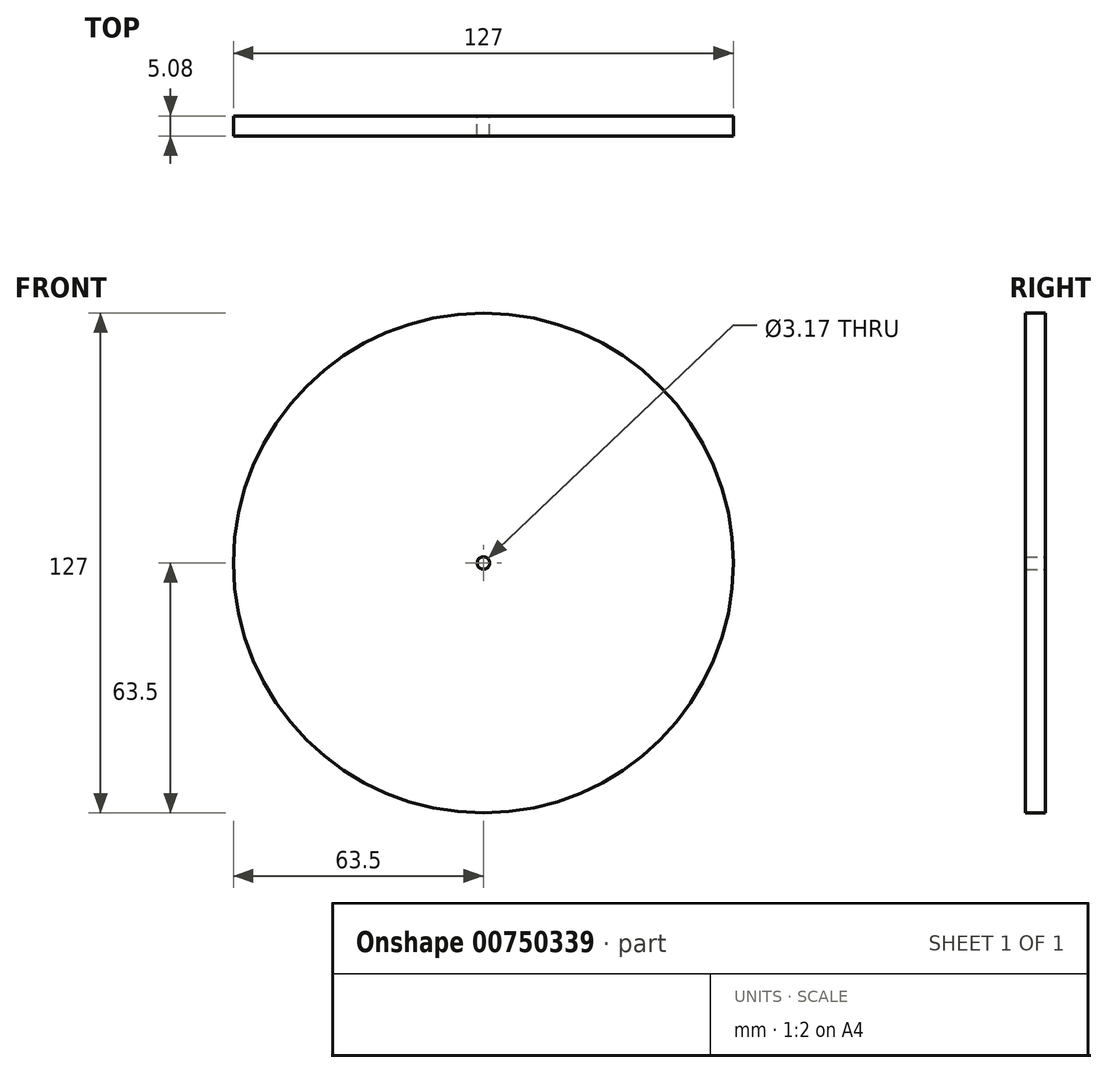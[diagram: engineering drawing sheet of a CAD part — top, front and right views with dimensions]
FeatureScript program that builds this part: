
annotation { "Feature Type Name" : "Feature", "Feature Type Description" : "" }
export const myFeature = defineFeature(function(context is Context, id is Id, definition is map)
    precondition{}
    {
        {
            var Q0;
            Q0=qCreatedBy(makeId("Front.planeOp"),FACE);
            var sketch = newSketch(context, id + "F0", { "sketchPlane" : qUnion([Q0])});
            skCircle(sketch, "E0", {"center": v(0, 0) * mm, "radius": 63.5 * mm});
            skCircle(sketch, "E1", {"center": v(0, 0) * mm, "radius": 1.59 * mm});
            skSolve(sketch);
        }
        {
            var Q0;
            Q0 = qSketchRegion(id + "F0", true);
            extrude(context, id + "F1", {"entities" : qUnion([Q0]), "depth" : 5.08 * mm, "offsetDistance" : 25.4 * mm});
        }
    });
